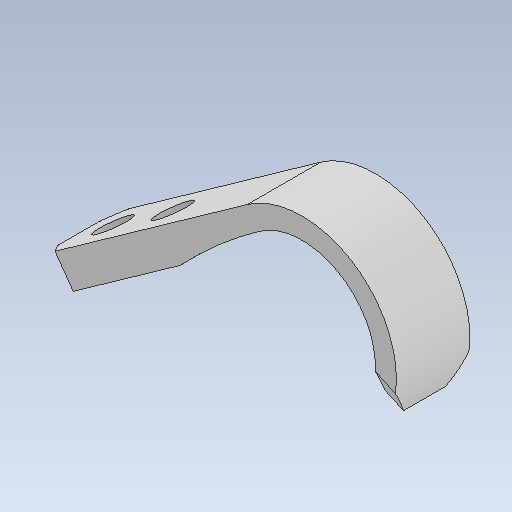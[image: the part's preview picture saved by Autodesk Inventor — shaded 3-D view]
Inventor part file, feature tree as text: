
AUTODESK INVENTOR PART (.ipt)
format: ipt  version: 2020 (Build 240168000, 168)  size: 121,856 bytes
history: native  units: mm
features: other x3, sketch x3, plane x1
ambient origin geometry x8: Origin, YZ Plane, XZ Plane, XY Plane, X Axis, Y Axis, Z Axis, Center Point
bodies: Solid1 (feature_tree)
feature tree (7):
  other  "foot_2.ipt"
  other  "Solid1::foot_2.ipt"
  other  "TaggingFeature1"
  sketch  "Sketch1"  dims[d0=10.0mm]
  sketch  "Sketch2"
  sketch  "Sketch3"
  plane  "Work Plane1"
